# Revit family: DCST_Счетчик водяной общедомовой_ОСВХ_Нептун
name_source: partatom
category: Арматура трубопроводов
units: mm (PartAtom-declared; Revit-internal decimal feet)

## family parameters
Всегда вертикально = Да
На основе рабочей плоскости = Нет
Общий = Нет
При загрузке вырезать с полостями = Нет
Размер круглого соединителя = Использовать диаметр
Тип детали = Вставляется

## types (3) — shared parameters
ADSK_Единица измерения = шт.
ADSK_Завод-изготовитель = Декаст
ADSK_Количество = 1
LT = ОСВХ_253240
URL = https://www.decast.com
Геркон = ♦ : импульсный выход (геркон)
Изготовитель = Декаст
Нет = ♦ : нет

## per-type parameters (varying)
| type | ADSK_Диаметр условный | D | D1 | DN2532 | DN40 | Dm | F | L1 | L2 | SW | Диаметр условного прохода | Монтажная длина | УГО_Высота | УГО_Длина | УГО_Длина линии |
| ОСВХ-25 "НЕПТУН" | 25 мм | 25 мм | 25 мм | Да | Нет | 30 мм | 10 мм | 43 мм | 22 мм | 45 мм | 25 мм | 170 мм | 97 мм | 194 мм | 43 мм |
| ОСВХ-32 "НЕПТУН" | 32 мм | 32 мм | 32 мм | Да | Нет | 40 мм | 8 мм | 63 мм | 25 мм | 55 мм | 32 мм | 170 мм | 100 мм | 200 мм | 63 мм |
| ОСВХ-40 "НЕПТУН" | 40 мм | 40 мм | 40 мм | Нет | Да | 45 мм | 13 мм | 63 мм | 25 мм | 65 мм | 40 мм | 190 мм | 110 мм | 220 мм | 63 мм |
